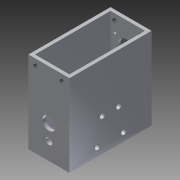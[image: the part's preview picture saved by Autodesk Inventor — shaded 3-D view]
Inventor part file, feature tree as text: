
AUTODESK INVENTOR PART (.ipt)
format: ipt  version: 2013 (Build 170138000, 138)  size: 198,144 bytes
history: native  units: mm
features: sketch x7, hole x5, thread x4, extrude x2, other x1
ambient origin geometry x1: Origin
feature tree (19):
  other  "ソリッド1"
  extrude  "押し出し1"  Depth=25.0mm
  extrude  "押し出し2"  Depth=50.0mm
  hole  "穴1"  [1 undecoded]
  hole  "穴2"  [1 undecoded]
  hole  "穴4"  [1 undecoded]
  thread  "ねじ1"
  thread  "ねじ2"
  thread  "ねじ3"
  thread  "ねじ4"
  hole  "穴5"  [1 undecoded]
  hole  "穴7"  [1 undecoded]
  sketch  "スケッチ1"
  sketch  "スケッチ2"
  sketch  "スケッチ3"
  sketch  "スケッチ4"
  sketch  "スケッチ5"
  sketch  "スケッチ7"
  sketch  "スケッチ8"
note: 5 required parameter values undecoded (feature->parameter linkage not recoverable at this tier; creation-order binding heuristic only, values carry confidence <= 0.55)
